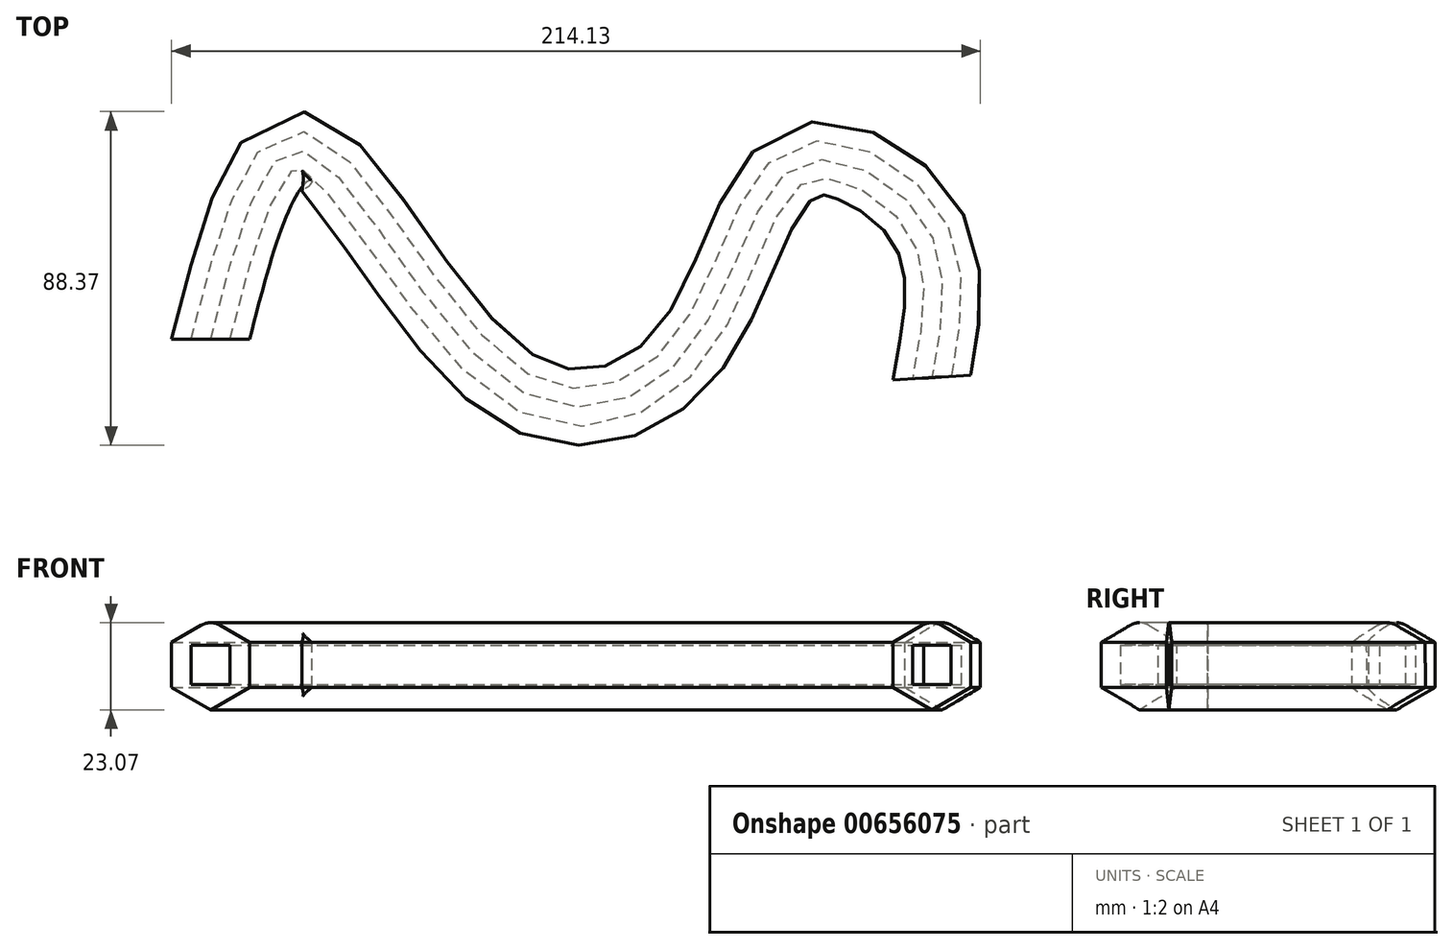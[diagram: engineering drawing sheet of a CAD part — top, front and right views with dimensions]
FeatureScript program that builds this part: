
annotation { "Feature Type Name" : "Feature", "Feature Type Description" : "" }
export const myFeature = defineFeature(function(context is Context, id is Id, definition is map)
    precondition{}
    {
        {
            var Q0;
            Q0=qCreatedBy(makeId("Top.planeOp"),FACE);
            var sketch = newSketch(context, id + "F0", { "sketchPlane" : qUnion([Q0])});
            skFitSpline(sketch, "E0", {"points": [v(-123.83, -13.48) * mm, v(-99.72, 36.45) * mm, v(-44.4, -25.67) * mm, v(3.26, -15.74) * mm, v(31.92, 32.77) * mm, v(65.1, 17.45) * mm, v(67.1, -23.69) * mm], "startDerivative": vector(116.46, 456.05) * mm, "endDerivative": vector(-55.36, -297.44) * mm});
            skSolve(sketch);
        }
        {
            var Q0;
            Q0=qCreatedBy(makeId("Front.planeOp"),FACE);
            var Q1;
            Q1=sQuery(id+"F0.wireOp",VERTEX,"E0.start");
            cPlane(context, id + "F1", {"entities" : qUnion([Q0, Q1]), "cplaneType" : CPlaneType.PLANE_POINT, "offset" : 25 * mm, "width" : 150 * mm, "height" : 150 * mm});
        }
        {
            var Q0;
            Q0=qCreatedBy(id+"F1.planeOp",FACE);
            var sketch = newSketch(context, id + "F2", { "sketchPlane" : qUnion([Q0])});
            skPoint(sketch, "E1.middle", {"position": v(-123.83, 0) * mm});
            skLineSegment(sketch, "E2.bottom", {"start": v(-118.68, -5.2) * mm, "end": v(-128.98, -5.2) * mm});
            skLineSegment(sketch, "E2.top", {"start": v(-118.68, 5.2) * mm, "end": v(-128.98, 5.2) * mm});
            skLineSegment(sketch, "E2.left", {"start": v(-118.68, -5.2) * mm, "end": v(-118.68, 5.2) * mm});
            skLineSegment(sketch, "E2.right", {"start": v(-128.98, -5.2) * mm, "end": v(-128.98, 5.2) * mm});
            skCircle(sketch, "E3.cCircle", {"center": v(-123.83, 0) * mm, "radius": 10.32 * mm, "construction": true});
            skLineSegment(sketch, "E3.0", {"start": v(-113.52, -5.98) * mm, "end": v(-123.85, -11.92) * mm});
            skLineSegment(sketch, "E3.1", {"start": v(-123.85, -11.92) * mm, "end": v(-134.16, -5.94) * mm});
            skLineSegment(sketch, "E3.2", {"start": v(-134.16, -5.94) * mm, "end": v(-134.14, 5.98) * mm});
            skLineSegment(sketch, "E3.3", {"start": v(-134.14, 5.98) * mm, "end": v(-126.31, 10.48) * mm});
            skLineSegment(sketch, "E3.4", {"start": v(-121.31, 10.47) * mm, "end": v(-113.5, 5.94) * mm});
            skLineSegment(sketch, "E3.5", {"start": v(-113.5, 5.94) * mm, "end": v(-113.52, -5.98) * mm});
            skPoint(sketch, "E3.0.midPoint", {"position": v(-118.68, -8.95) * mm});
            skPoint(sketch, "E4.visualSharp", {"position": v(-123.81, 11.92) * mm});
            skArc(sketch, "E4.filletArc", {"start": v(-121.31, 10.47) * mm, "mid": v(-123.81, 11.15) * mm, "end": v(-126.31, 10.48) * mm});
            skLineSegment(sketch, "E5", {"start": v(-184.54, 0.34) * mm, "end": v(-178.85, 14.47) * mm});
            skLineSegment(sketch, "E6", {"start": v(-165.56, 30.76) * mm, "end": v(-156.98, 24.46) * mm});
            skArc(sketch, "E7.filletArc", {"start": v(-165.56, 30.76) * mm, "mid": v(-169.88, 31.54) * mm, "end": v(-173.15, 28.6) * mm});
            skFitSpline(sketch, "E8", {"points": [v(-145.61, 32.31) * mm, v(-125.94, 55.11) * mm, v(-104.44, 59.66) * mm, v(-91.33, 31.07) * mm], "startDerivative": vector(47.14, 70.28) * mm, "endDerivative": vector(33.54, -71.9) * mm});
            skFitSpline(sketch, "E9", {"points": [v(-104.58, 31.91) * mm, v(-126.18, 31.07) * mm, v(-147.07, 47.36) * mm, v(-168.35, 48.9) * mm], "startDerivative": vector(-42.23, 43.4) * mm, "endDerivative": vector(-66.4, -22.6) * mm});
            skLineSegment(sketch, "E10", {"start": v(-156.98, 24.46) * mm, "end": v(-148.4, 18.16) * mm});
            skLineSegment(sketch, "E11", {"start": v(-178.85, 14.47) * mm, "end": v(-173.24, 28.37) * mm});
            skLineSegment(sketch, "E12", {"start": v(-173.24, 28.37) * mm, "end": v(-173.15, 28.6) * mm});
            skLineSegment(sketch, "E13.top", {"start": v(-172.08, -48.37) * mm, "end": v(-132.25, -48.37) * mm});
            skLineSegment(sketch, "E13.right", {"start": v(-132.25, -22.35) * mm, "end": v(-132.25, -48.37) * mm});
            skLineSegment(sketch, "E14", {"start": v(-163.61, -22.35) * mm, "end": v(-132.25, -22.35) * mm});
            skLineSegment(sketch, "E15", {"start": v(-172.08, -29.07) * mm, "end": v(-172.08, -48.37) * mm});
            skSolve(sketch);
        }
        {
            var Q0;
            Q0=makeQuery(id+"F2.imprint","IMPRINT",FACE,{"disambiguationData":[TD([[makeQuery(id+"F2.imprint","IMPRINT",EDGE,{"derivedFrom":sQuery(id+"F2.wireOp",EDGE,"E2.bottom")}),1.0]])]});
            var Q1;
            Q1=sQuery(id+"F0.wireOp",EDGE,"E0");
            sweep(context, id + "F3", {"profiles" : qUnion([Q0]), "path" : qUnion([Q1])});
        }
    });
